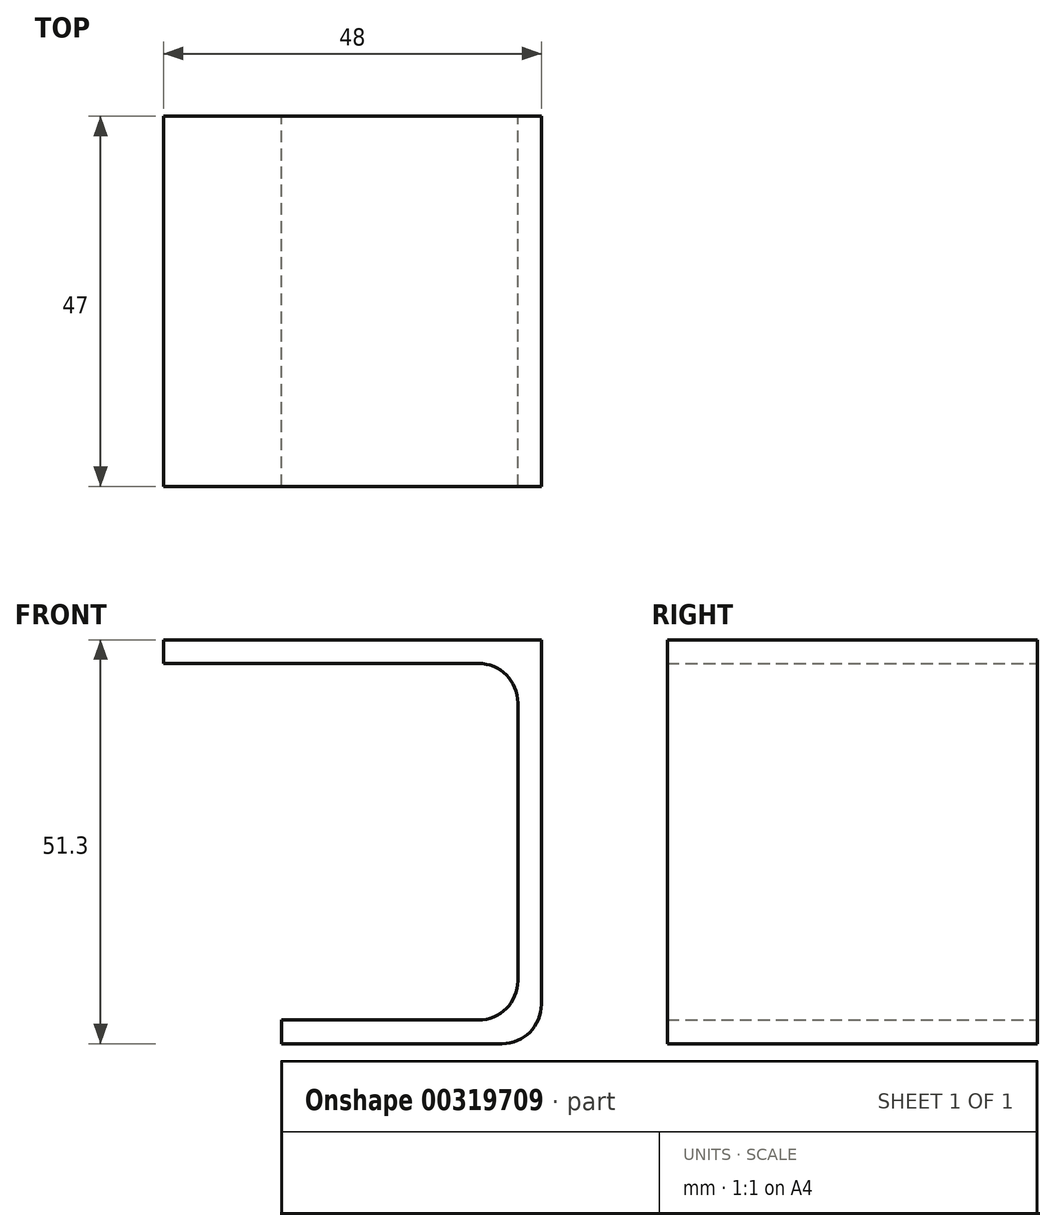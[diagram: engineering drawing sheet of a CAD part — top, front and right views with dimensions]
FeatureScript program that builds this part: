
annotation { "Feature Type Name" : "Feature", "Feature Type Description" : "" }
export const myFeature = defineFeature(function(context is Context, id is Id, definition is map)
    precondition{}
    {
        {
            var Q0;
            Q0=qCreatedBy(makeId("Front.planeOp"),FACE);
            var sketch = newSketch(context, id + "F0", { "sketchPlane" : qUnion([Q0])});
            skLineSegment(sketch, "E0", {"start": v(-44.81, 51.3) * mm, "end": v(-44.81, 48.3) * mm});
            skLineSegment(sketch, "E1", {"start": v(-44.81, 48.3) * mm, "end": v(-14.81, 48.3) * mm});
            skLineSegment(sketch, "E2", {"start": v(-14.81, 48.3) * mm, "end": v(-14.81, 3) * mm});
            skLineSegment(sketch, "E3", {"start": v(-14.81, 3) * mm, "end": v(-44.81, 3) * mm});
            skLineSegment(sketch, "E4", {"start": v(-44.81, 3) * mm, "end": v(-44.81, 0) * mm});
            skLineSegment(sketch, "E5", {"start": v(-44.81, 0) * mm, "end": v(-11.81, 0) * mm});
            skLineSegment(sketch, "E6", {"start": v(-11.81, 0) * mm, "end": v(-11.81, 51.3) * mm});
            skLineSegment(sketch, "E7", {"start": v(-11.81, 51.3) * mm, "end": v(-44.81, 51.3) * mm});
            skSolve(sketch);
        }
        {
            var Q0;
            Q0 = qSketchRegion(id + "F0", true);
            extrude(context, id + "F1", {"entities" : qUnion([Q0]), "depth" : 47 * mm});
        }
        {
            var Q0;
            Q0=makeQuery(id+"F1.opExtrude","SWEPT_EDGE",EDGE,{"disambiguationData":[OSD([sQuery(id+"F0.wireOp",EDGE,"E2"),sQuery(id+"F0.wireOp",EDGE,"E3")])]});
            var Q1;
            Q1=makeQuery(id+"F1.opExtrude","SWEPT_EDGE",EDGE,{"disambiguationData":[OSD([sQuery(id+"F0.wireOp",EDGE,"E1"),sQuery(id+"F0.wireOp",EDGE,"E2")])]});
            fillet(context, id + "F2", {"entities" : qUnion([Q0, Q1]), "radius" : 5 * mm, "tangentPropagation" : true, "allowEdgeOverflow" : false});
        }
        {
            var Q0;
            Q0=makeQuery(id+"F1.opExtrude","SWEPT_EDGE",EDGE,{"disambiguationData":[OSD([sQuery(id+"F0.wireOp",EDGE,"E5"),sQuery(id+"F0.wireOp",EDGE,"E6")])]});
            fillet(context, id + "F3", {"entities" : qUnion([Q0]), "radius" : 5 * mm, "tangentPropagation" : true, "allowEdgeOverflow" : false});
        }
        {
            var Q0;
            Q0=makeQuery(id+"F1.opExtrude","SWEPT_FACE",FACE,{"disambiguationData":[OSD([sQuery(id+"F0.wireOp",EDGE,"E0")])]});
            extrude(context, id + "F4", {"entities" : qUnion([Q0]), "operationType" : NewBodyOperationType.ADD, "depth" : 15 * mm, "offsetDistance" : 25 * mm});
        }
    });
